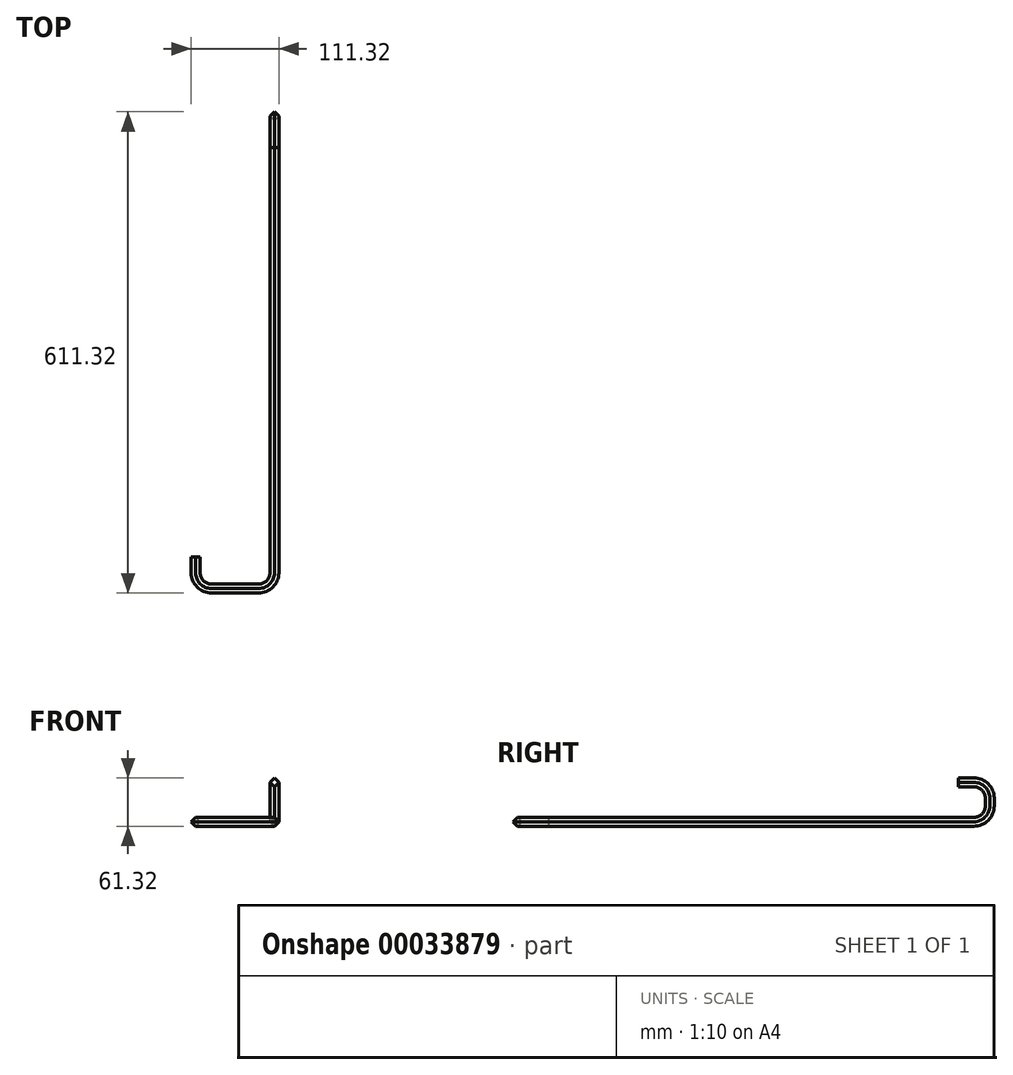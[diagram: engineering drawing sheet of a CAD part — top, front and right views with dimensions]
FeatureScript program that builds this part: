
annotation { "Feature Type Name" : "Feature", "Feature Type Description" : "" }
export const myFeature = defineFeature(function(context is Context, id is Id, definition is map)
    precondition{}
    {
        {
            var Q0;
            Q0=qCreatedBy(makeId("Top.planeOp"),FACE);
            var sketch = newSketch(context, id + "F0", { "sketchPlane" : qUnion([Q0])});
            skLineSegment(sketch, "E0", {"start": v(0, 0) * mm, "end": v(0, -20) * mm});
            skLineSegment(sketch, "E1", {"start": v(20, -40) * mm, "end": v(80, -40) * mm});
            skLineSegment(sketch, "E2", {"start": v(100, -20) * mm, "end": v(100, 540) * mm});
            skPoint(sketch, "E3.visualSharp", {"position": v(0, -40) * mm});
            skArc(sketch, "E3.filletArc", {"start": v(0, -20) * mm, "mid": v(5.86, -34.14) * mm, "end": v(20, -40) * mm});
            skPoint(sketch, "E4.visualSharp", {"position": v(100, -40) * mm});
            skArc(sketch, "E4.filletArc", {"start": v(80, -40) * mm, "mid": v(94.14, -34.14) * mm, "end": v(100, -20) * mm});
            skSolve(sketch);
        }
        {
            var Q0;
            Q0=sQuery(id+"F0.wireOp",EDGE,"E2");
            cPlane(context, id + "F1", {"entities" : qUnion([Q0]), "cplaneType" : CPlaneType.LINE_ANGLE, "offset" : 150 * mm, "angle" : 90 * degree, "width" : 150 * mm, "height" : 150 * mm});
        }
        {
            var Q0;
            Q0=qCreatedBy(id+"F1.planeOp",FACE);
            var sketch = newSketch(context, id + "F2", { "sketchPlane" : qUnion([Q0])});
            skArc(sketch, "E5", {"start": v(540, 0) * mm, "mid": v(554.14, 5.86) * mm, "end": v(560, 20) * mm});
            skLineSegment(sketch, "E6", {"start": v(560, 20) * mm, "end": v(560, 30) * mm});
            skLineSegment(sketch, "E7", {"start": v(540, 50) * mm, "end": v(520, 50) * mm});
            skPoint(sketch, "E8.visualSharp", {"position": v(560, 50) * mm});
            skArc(sketch, "E8.filletArc", {"start": v(560, 30) * mm, "mid": v(554.14, 44.14) * mm, "end": v(540, 50) * mm});
            skSolve(sketch);
        }
        {
            var Q0;
            Q0=qCreatedBy(makeId("Front.planeOp"),FACE);
            var sketch = newSketch(context, id + "F3", { "sketchPlane" : qUnion([Q0])});
            skLineSegment(sketch, "E9", {"start": v(5.66, 0) * mm, "end": v(0, -5.66) * mm});
            skLineSegment(sketch, "E10", {"start": v(0, -5.66) * mm, "end": v(-5.66, 0) * mm});
            skLineSegment(sketch, "E11", {"start": v(-5.66, 0) * mm, "end": v(0, 5.66) * mm});
            skLineSegment(sketch, "E12", {"start": v(0, 5.66) * mm, "end": v(5.66, 0) * mm});
            skSolve(sketch);
        }
        {
            var Q0;
            Q0=makeQuery(id+"F3.imprint","IMPRINT",FACE,{"disambiguationData":[TD([[makeQuery(id+"F3.imprint","IMPRINT",EDGE,{"derivedFrom":sQuery(id+"F3.wireOp",EDGE,"E9")}),-1.0]])]});
            var Q1;
            Q1=sQuery(id+"F0.wireOp",EDGE,"E0");
            var Q2;
            Q2=sQuery(id+"F0.wireOp",EDGE,"E3.filletArc");
            var Q3;
            Q3=sQuery(id+"F0.wireOp",EDGE,"E1");
            var Q4;
            Q4=sQuery(id+"F0.wireOp",EDGE,"E4.filletArc");
            var Q5;
            Q5=sQuery(id+"F0.wireOp",EDGE,"E2");
            var Q6;
            Q6=sQuery(id+"F2.wireOp",EDGE,"E5");
            var Q7;
            Q7=sQuery(id+"F2.wireOp",EDGE,"E6");
            var Q8;
            Q8=sQuery(id+"F2.wireOp",EDGE,"E8.filletArc");
            var Q9;
            Q9=sQuery(id+"F2.wireOp",EDGE,"E7");
            sweep(context, id + "F4", {"profiles" : qUnion([Q0]), "path" : qUnion([Q1, Q2, Q3, Q4, Q5, Q6, Q7, Q8, Q9])});
        }
    });
